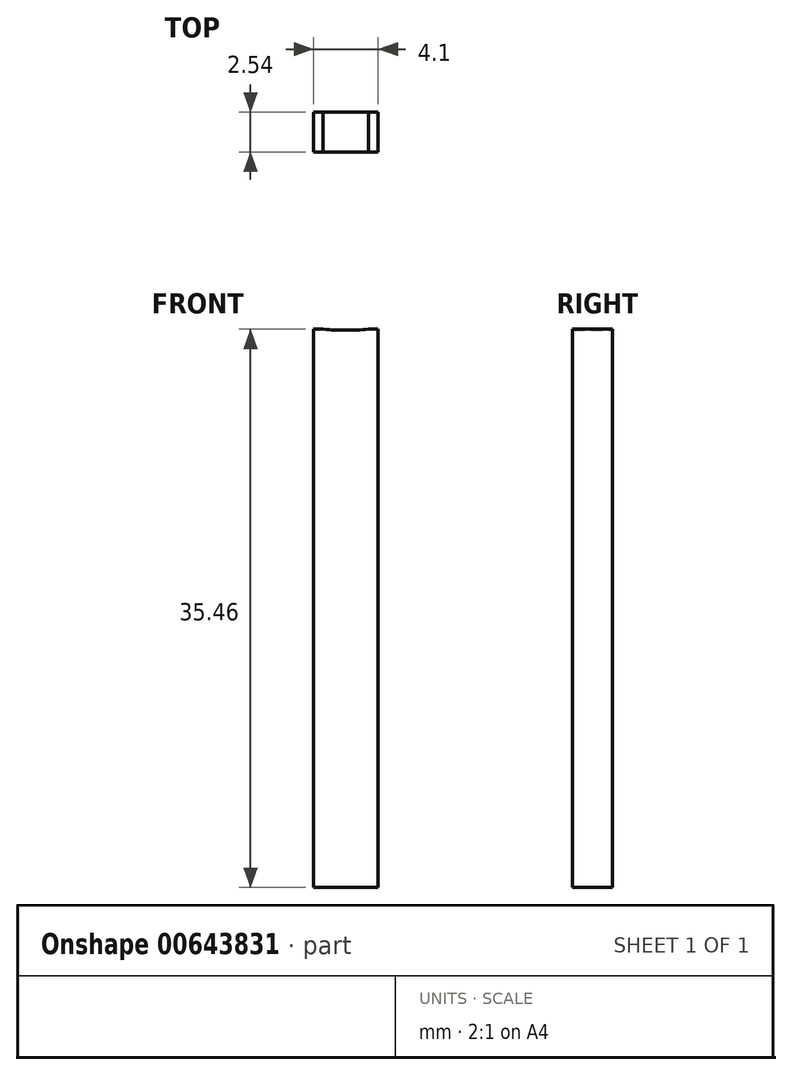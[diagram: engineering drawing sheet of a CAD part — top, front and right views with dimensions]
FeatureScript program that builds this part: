
annotation { "Feature Type Name" : "Feature", "Feature Type Description" : "" }
export const myFeature = defineFeature(function(context is Context, id is Id, definition is map)
    precondition{}
    {
        {
            var Q0;
            Q0=qCreatedBy(makeId("Front.planeOp"),FACE);
            var sketch = newSketch(context, id + "F0", { "sketchPlane" : qUnion([Q0])});
            skLineSegment(sketch, "E0.bottom", {"start": v(2.05, -17.73) * mm, "end": v(-2.05, -17.73) * mm});
            skLineSegment(sketch, "E0.top", {"start": v(2.05, 17.73) * mm, "end": v(-2.05, 17.73) * mm});
            skLineSegment(sketch, "E0.left", {"start": v(2.05, -17.73) * mm, "end": v(2.05, 17.73) * mm});
            skLineSegment(sketch, "E0.right", {"start": v(-2.05, -17.73) * mm, "end": v(-2.05, 17.73) * mm});
            skPoint(sketch, "E0.middle", {"position": v(0, 0) * mm});
            skCircle(sketch, "E1", {"center": v(0, 33.63) * mm, "radius": 15.96 * mm});
            skSolve(sketch);
        }
        {
            var Q0;
            {var subQ0=sQuery(id+"F0.wireOp",EDGE,"E1");var subQ1=sQuery(id+"F0.wireOp",EDGE,"E0.top");var subQ2=makeQuery(id+"F0.imprint","INTERSECT",VERTEX,{"disambiguationData":[OD(0.0)],"derivedFrom":[subQ1,subQ0]});Q0=makeQuery(id+"F0.imprint","IMPRINT",FACE,{"disambiguationData":[TD([[makeQuery(id+"F0.imprint","IMPRINT",EDGE,{"disambiguationData":[TD([[subQ2,-1.0]])],"derivedFrom":subQ1}),-1.0]])]});}
            var Q1;
            Q1=makeQuery(id+"F0.imprint","IMPRINT",FACE,{"disambiguationData":[TD([[makeQuery(id+"F0.imprint","IMPRINT",EDGE,{"derivedFrom":sQuery(id+"F0.wireOp",EDGE,"E0.bottom")}),-1.0]])]});
            extrude(context, id + "F1", {"entities" : qUnion([Q0, Q1]), "depth" : 2.54 * mm, "offsetDistance" : 25.4 * mm});
        }
        {
            var Q0;
            Q0=makeQuery(id+"F1.opExtrude","CAP_FACE",FACE,{"disambiguationData":[OSD([sQuery(id+"F0.wireOp",EDGE,"E0.top"),sQuery(id+"F0.wireOp",EDGE,"E1")])],"isStart":false});
            var sketch = newSketch(context, id + "F2", { "sketchPlane" : qUnion([Q0])});
            skPoint(sketch, "E2", {"position": v(0, 33.63) * mm});
            skSolve(sketch);
        }
        {
            var Q0;
            Q0=sQuery(id+"F2.wireOp",VERTEX,"E2");
            var Q1;
            Q1=makeQuery(id+"F1.opExtrude","SWEPT_BODY",BODY,{"disambiguationData":[OSD([sQuery(id+"F0.wireOp",EDGE,"E0.top"),sQuery(id+"F0.wireOp",EDGE,"E1")])]});
            hole(context, id + "F3", {"style" : HoleStyle.SIMPLE, "endStyle" : HoleEndStyle.THROUGH, "holeDiameter" : 25.4 * mm, "majorDiameter" : 6.35 * mm, "isTappedThrough" : true, "tappedDepth" : 12.7 * mm, "tapClearance" : 3, "startFromSketch" : true, "locations" : qUnion([Q0]), "scope" : qUnion([Q1])});
        }
    });
